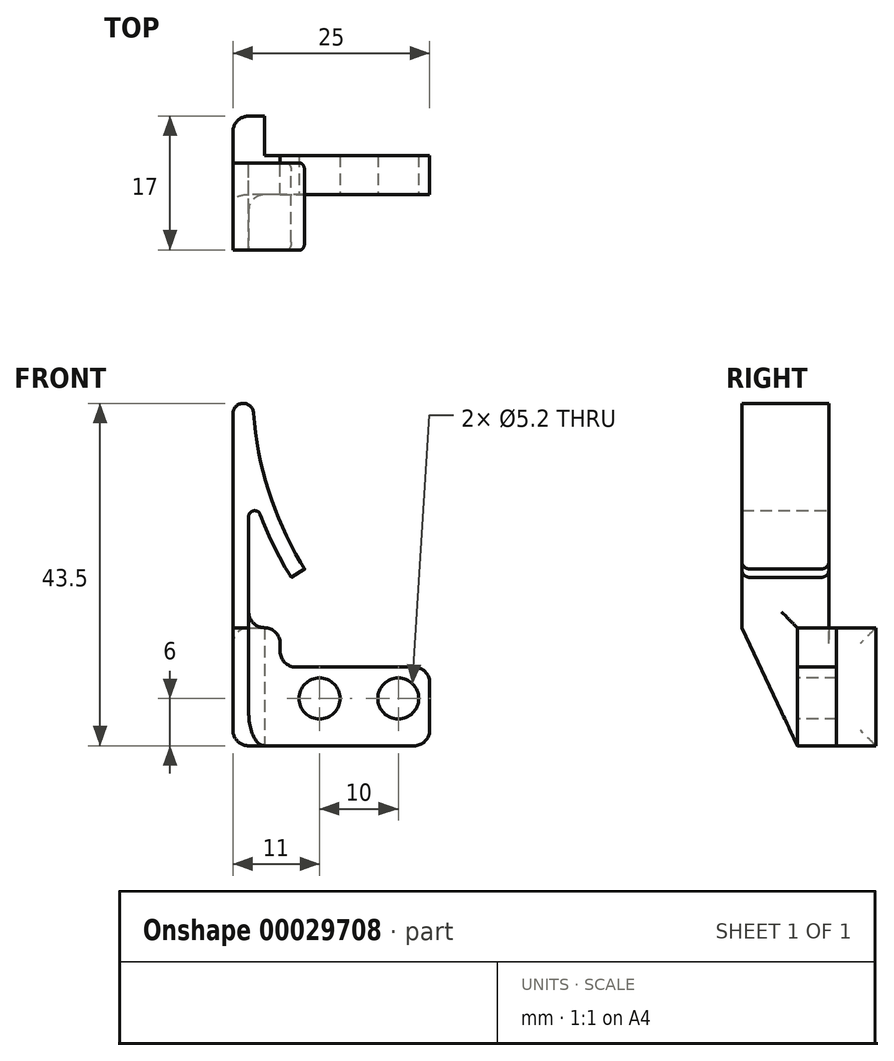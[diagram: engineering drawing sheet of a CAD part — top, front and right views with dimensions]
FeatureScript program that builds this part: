
annotation { "Feature Type Name" : "Feature", "Feature Type Description" : "" }
export const myFeature = defineFeature(function(context is Context, id is Id, definition is map)
    precondition{}
    {
        {
            var Q0;
            Q0=qCreatedBy(makeId("Front.planeOp"),FACE);
            var sketch = newSketch(context, id + "F0", { "sketchPlane" : qUnion([Q0])});
            skLineSegment(sketch, "E0", {"start": v(0, 0) * mm, "end": v(0, 42.19) * mm});
            skLineSegment(sketch, "E1", {"start": v(25, 0) * mm, "end": v(0, 0) * mm});
            skLineSegment(sketch, "E2", {"start": v(2, 29.11) * mm, "end": v(2, 15) * mm});
            skLineSegment(sketch, "E3", {"start": v(2, 15) * mm, "end": v(6, 15) * mm});
            skLineSegment(sketch, "E4", {"start": v(6, 15) * mm, "end": v(6, 10) * mm});
            skLineSegment(sketch, "E5", {"start": v(6, 10) * mm, "end": v(25, 10) * mm});
            skLineSegment(sketch, "E6", {"start": v(46, 0) * mm, "end": v(46, 45.5) * mm, "construction": true});
            skLineSegment(sketch, "E7", {"start": v(46, 45.5) * mm, "end": v(0, 45.5) * mm, "construction": true});
            skLineSegment(sketch, "E8", {"start": v(25, 10) * mm, "end": v(25, 0) * mm});
            skArc(sketch, "E9", {"start": v(2.62, 42.29) * mm, "mid": v(4.66, 31.97) * mm, "end": v(9.1, 22.45) * mm});
            skLineSegment(sketch, "E10", {"start": v(46, 45.5) * mm, "end": v(9.1, 22.45) * mm, "construction": true});
            skArc(sketch, "E11", {"start": v(2.62, 42.29) * mm, "mid": v(1.26, 43.5) * mm, "end": v(0, 42.19) * mm});
            skArc(sketch, "E12", {"start": v(3.45, 29.38) * mm, "mid": v(5.24, 25.29) * mm, "end": v(7.41, 21.39) * mm});
            skLineSegment(sketch, "E13", {"start": v(9.1, 22.45) * mm, "end": v(7.41, 21.39) * mm});
            skLineSegment(sketch, "E14", {"start": v(2.75, 29.11) * mm, "end": v(46, 45.5) * mm, "construction": true});
            skLineSegment(sketch, "E15", {"start": v(2.75, 29.11) * mm, "end": v(46, 29.11) * mm, "construction": true});
            skArc(sketch, "E16", {"start": v(3.45, 29.38) * mm, "mid": v(2.61, 29.85) * mm, "end": v(2, 29.11) * mm});
            skLineSegment(sketch, "E17", {"start": v(1.31, 42.19) * mm, "end": v(46, 45.5) * mm, "construction": true});
            skLineSegment(sketch, "E18", {"start": v(1.31, 42.19) * mm, "end": v(46, 42.19) * mm, "construction": true});
            skSolve(sketch);
        }
        {
            var Q0;
            Q0=makeQuery(id+"F0.imprint","IMPRINT",FACE,{"disambiguationData":[TD([[makeQuery(id+"F0.imprint","IMPRINT",EDGE,{"derivedFrom":sQuery(id+"F0.wireOp",EDGE,"E0")}),-1.0]])]});
            extrude(context, id + "F1", {"entities" : qUnion([Q0]), "depth" : 12 * mm});
        }
        {
            var Q0;
            Q0=makeQuery(id+"F1.opExtrude","CAP_FACE",FACE,{"disambiguationData":[OSD([sQuery(id+"F0.wireOp",EDGE,"E0"),sQuery(id+"F0.wireOp",EDGE,"b13cdfa3-eb26-4a5b-9c51-0565e7d605f8"),sQuery(id+"F0.wireOp",EDGE,"20c8e588-8513-4586-873b-a1e2a7cb5edc"),sQuery(id+"F0.wireOp",EDGE,"99ee8a31-633d-4312-811c-a954296da4b5"),sQuery(id+"F0.wireOp",EDGE,"e968206b-c05c-4754-84ed-d64e79b235ea"),sQuery(id+"F0.wireOp",EDGE,"b45f21d6-cdd7-40ae-9b71-acff4328d14c"),sQuery(id+"F0.wireOp",EDGE,"3f474ec2-51ba-4bb6-b08a-34516dbad5d3"),sQuery(id+"F0.wireOp",EDGE,"E1"),sQuery(id+"F0.wireOp",EDGE,"086c25bb-8a97-4a79-a392-a81f9e8244d4.filletArc"),sQuery(id+"F0.wireOp",EDGE,"f96bd52e-1912-4527-b69c-6590beda2ba5.filletArc")])],"isStart":false});
            var sketch = newSketch(context, id + "F2", { "sketchPlane" : qUnion([Q0])});
            skPoint(sketch, "E19", {"position": v(11, 6) * mm});
            skPoint(sketch, "E20", {"position": v(21, 6) * mm});
            skSolve(sketch);
        }
        {
            var Q0;
            Q0=sQuery(id+"F2.wireOp",VERTEX,"E20");
            var Q1;
            Q1=sQuery(id+"F2.wireOp",VERTEX,"E19");
            var Q2;
            Q2=makeQuery(id+"F1.opExtrude","SWEPT_BODY",BODY,{"disambiguationData":[OSD([sQuery(id+"F0.wireOp",EDGE,"E0"),sQuery(id+"F0.wireOp",EDGE,"b13cdfa3-eb26-4a5b-9c51-0565e7d605f8"),sQuery(id+"F0.wireOp",EDGE,"20c8e588-8513-4586-873b-a1e2a7cb5edc"),sQuery(id+"F0.wireOp",EDGE,"99ee8a31-633d-4312-811c-a954296da4b5"),sQuery(id+"F0.wireOp",EDGE,"3f474ec2-51ba-4bb6-b08a-34516dbad5d3"),sQuery(id+"F0.wireOp",EDGE,"E1"),sQuery(id+"F0.wireOp",EDGE,"086c25bb-8a97-4a79-a392-a81f9e8244d4.filletArc"),sQuery(id+"F0.wireOp",EDGE,"f96bd52e-1912-4527-b69c-6590beda2ba5.filletArc"),sQuery(id+"F0.wireOp",EDGE,"E2"),sQuery(id+"F0.wireOp",EDGE,"E3"),sQuery(id+"F0.wireOp",EDGE,"E4"),sQuery(id+"F0.wireOp",EDGE,"E5")])]});
            hole(context, id + "F3", {"style" : HoleStyle.SIMPLE, "holeDiameter" : 5.2 * mm, "endStyle" : HoleEndStyle.THROUGH, "locations" : qUnion([Q0, Q1]), "scope" : qUnion([Q2])});
        }
        {
            var Q0;
            Q0=makeQuery(id+"F1.opExtrude","CAP_FACE",FACE,{"disambiguationData":[OSD([sQuery(id+"F0.wireOp",EDGE,"E0"),sQuery(id+"F0.wireOp",EDGE,"b13cdfa3-eb26-4a5b-9c51-0565e7d605f8"),sQuery(id+"F0.wireOp",EDGE,"20c8e588-8513-4586-873b-a1e2a7cb5edc"),sQuery(id+"F0.wireOp",EDGE,"99ee8a31-633d-4312-811c-a954296da4b5"),sQuery(id+"F0.wireOp",EDGE,"3f474ec2-51ba-4bb6-b08a-34516dbad5d3"),sQuery(id+"F0.wireOp",EDGE,"E1"),sQuery(id+"F0.wireOp",EDGE,"086c25bb-8a97-4a79-a392-a81f9e8244d4.filletArc"),sQuery(id+"F0.wireOp",EDGE,"f96bd52e-1912-4527-b69c-6590beda2ba5.filletArc"),sQuery(id+"F0.wireOp",EDGE,"E2"),sQuery(id+"F0.wireOp",EDGE,"E3"),sQuery(id+"F0.wireOp",EDGE,"E4"),sQuery(id+"F0.wireOp",EDGE,"E5")])],"isStart":false});
            var sketch = newSketch(context, id + "F4", { "sketchPlane" : qUnion([Q0])});
            skLineSegment(sketch, "E21.bottom", {"start": v(2, 0) * mm, "end": v(0, 0) * mm});
            skLineSegment(sketch, "E21.top", {"start": v(2, 15) * mm, "end": v(0, 15) * mm});
            skLineSegment(sketch, "E21.left", {"start": v(0, 0) * mm, "end": v(0, 15) * mm});
            skLineSegment(sketch, "E21.right", {"start": v(2, 0) * mm, "end": v(2, 15) * mm});
            skSolve(sketch);
        }
        {
            var Q0;
            {var subQ2=sQuery(id+"F4.wireOp",EDGE,"E21.right");Q0=makeQuery(id+"F4.imprint","IMPRINT",FACE,{"disambiguationData":[TD([[makeQuery(id+"F4.imprint","IMPRINT",EDGE,{"derivedFrom":subQ2}),-1.0]])]});}
            extrude(context, id + "F5", {"entities" : qUnion([Q0]), "operationType" : NewBodyOperationType.REMOVE, "oppositeDirection" : true, "depth" : 7 * mm});
        }
        {
            var Q0;
            Q0=makeQuery(id+"F1.opExtrude","SWEPT_FACE",FACE,{"disambiguationData":[OSD([sQuery(id+"F0.wireOp",EDGE,"E0")])]});
            var sketch = newSketch(context, id + "F6", { "sketchPlane" : qUnion([Q0])});
            skLineSegment(sketch, "E22", {"start": v(12, 0) * mm, "end": v(12, 15) * mm});
            skLineSegment(sketch, "E23", {"start": v(12, 15) * mm, "end": v(5, 0) * mm});
            skLineSegment(sketch, "E24", {"start": v(5, 0) * mm, "end": v(12, 0) * mm});
            skSolve(sketch);
        }
        {
            var Q0;
            Q0 = qSketchRegion(id + "F6", true);
            var Q1;
            Q1=makeQuery(id+"F6.imprint","IMPRINT",FACE,{"disambiguationData":[TD([[makeQuery(id+"F6.imprint","IMPRINT",EDGE,{"derivedFrom":sQuery(id+"F6.wireOp",EDGE,"E22")}),1.0]])]});
            extrude(context, id + "F7", {"entities" : qUnion([Q0, Q1]), "operationType" : NewBodyOperationType.REMOVE, "oppositeDirection" : true, "depth" : 3 * mm});
        }
        {
            var Q0;
            Q0=qCreatedBy(makeId("Front.planeOp"),FACE);
            var sketch = newSketch(context, id + "F8", { "sketchPlane" : qUnion([Q0])});
            skLineSegment(sketch, "E25.bottom", {"start": v(-9.17, 45.96) * mm, "end": v(17.7, 45.96) * mm});
            skLineSegment(sketch, "E25.top", {"start": v(-9.17, 15) * mm, "end": v(17.7, 15) * mm});
            skLineSegment(sketch, "E25.left", {"start": v(-9.17, 45.96) * mm, "end": v(-9.17, 15) * mm});
            skLineSegment(sketch, "E25.right", {"start": v(17.7, 45.96) * mm, "end": v(17.7, 15) * mm});
            skSolve(sketch);
        }
        {
            var Q0;
            Q0=makeQuery(id+"F8.imprint","IMPRINT",FACE,{"disambiguationData":[TD([[makeQuery(id+"F8.imprint","IMPRINT",EDGE,{"derivedFrom":sQuery(id+"F8.wireOp",EDGE,"E25.bottom")}),-1.0]])]});
            extrude(context, id + "F9", {"entities" : qUnion([Q0]), "operationType" : NewBodyOperationType.REMOVE, "depth" : 1 * mm});
        }
        {
            var Q0;
            Q0=makeQuery(id+"F1.opExtrude","CAP_FACE",FACE,{"disambiguationData":[OSD([sQuery(id+"F0.wireOp",EDGE,"E0"),sQuery(id+"F0.wireOp",EDGE,"E1"),sQuery(id+"F0.wireOp",EDGE,"E2"),sQuery(id+"F0.wireOp",EDGE,"E3"),sQuery(id+"F0.wireOp",EDGE,"E4"),sQuery(id+"F0.wireOp",EDGE,"E5"),sQuery(id+"F0.wireOp",EDGE,"E8"),sQuery(id+"F0.wireOp",EDGE,"E9"),sQuery(id+"F0.wireOp",EDGE,"E11"),sQuery(id+"F0.wireOp",EDGE,"E12"),sQuery(id+"F0.wireOp",EDGE,"E13"),sQuery(id+"F0.wireOp",EDGE,"E16")])],"isStart":true});
            var sketch = newSketch(context, id + "F10", { "sketchPlane" : qUnion([Q0])});
            skLineSegment(sketch, "E26.bottom", {"start": v(0, 15) * mm, "end": v(-4, 15) * mm});
            skLineSegment(sketch, "E26.top", {"start": v(0, 0) * mm, "end": v(-4, 0) * mm});
            skLineSegment(sketch, "E26.left", {"start": v(0, 15) * mm, "end": v(0, 0) * mm});
            skLineSegment(sketch, "E26.right", {"start": v(-4, 15) * mm, "end": v(-4, 0) * mm});
            skSolve(sketch);
        }
        {
            var Q0;
            {var subQ4=sQuery(id+"F10.wireOp",EDGE,"E26.bottom");Q0=makeQuery(id+"F10.imprint","IMPRINT",FACE,{"disambiguationData":[TD([[makeQuery(id+"F10.imprint","IMPRINT",EDGE,{"derivedFrom":subQ4}),1.0]])]});}
            extrude(context, id + "F11", {"entities" : qUnion([Q0]), "operationType" : NewBodyOperationType.ADD, "depth" : 5 * mm});
        }
        {
            var Q0;
            Q0=makeQuery(id+"F1.opExtrude","CAP_EDGE",EDGE,{"disambiguationData":[OSD([sQuery(id+"F0.wireOp",EDGE,"E13")])],"isStart":false});
            var Q1;
            Q1=makeQuery(id+"F9.boolean.opBoolean","INTERSECT",EDGE,{"derivedFrom":[makeQuery(id+"F1.opExtrude","SWEPT_FACE",FACE,{"disambiguationData":[OSD([sQuery(id+"F0.wireOp",EDGE,"E13")])]}),makeQuery(id+"F9.opExtrude","CAP_FACE",FACE,{"disambiguationData":[OSD([sQuery(id+"F8.wireOp",EDGE,"E25.bottom"),sQuery(id+"F8.wireOp",EDGE,"E25.top"),sQuery(id+"F8.wireOp",EDGE,"E25.left"),sQuery(id+"F8.wireOp",EDGE,"E25.right")])],"isStart":false})]});
            fillet(context, id + "F12", {"entities" : qUnion([Q0, Q1]), "radius" : 1 * mm, "tangentPropagation" : true, "allowEdgeOverflow" : false});
        }
        {
            var Q0;
            Q0=makeQuery(id+"F1.opExtrude","SWEPT_EDGE",EDGE,{"disambiguationData":[OSD([sQuery(id+"F0.wireOp",EDGE,"E0"),sQuery(id+"F0.wireOp",EDGE,"E1")])]});
            var Q1;
            Q1=makeQuery(id+"F1.opExtrude","SWEPT_EDGE",EDGE,{"disambiguationData":[OSD([sQuery(id+"F0.wireOp",EDGE,"E1"),sQuery(id+"F0.wireOp",EDGE,"E8")])]});
            var Q2;
            Q2=makeQuery(id+"F1.opExtrude","SWEPT_EDGE",EDGE,{"disambiguationData":[OSD([sQuery(id+"F0.wireOp",EDGE,"E5"),sQuery(id+"F0.wireOp",EDGE,"E8")])]});
            var Q3;
            Q3=makeQuery(id+"F7.boolean.opBoolean","COPY",EDGE,{"derivedFrom":makeQuery(id+"F7.opExtrude","SWEPT_EDGE",EDGE,{"disambiguationData":[OSD([sQuery(id+"F0.wireOp",EDGE,"E0"),sQuery(id+"F6.wireOp",EDGE,"E22"),sQuery(id+"F6.wireOp",EDGE,"E23")])]})});
            var Q4;
            Q4=makeQuery(id+"F1.opExtrude","SWEPT_EDGE",EDGE,{"disambiguationData":[OSD([sQuery(id+"F0.wireOp",EDGE,"E3"),sQuery(id+"F0.wireOp",EDGE,"E4")])]});
            var Q5;
            Q5=makeQuery(id+"F1.opExtrude","SWEPT_EDGE",EDGE,{"disambiguationData":[OSD([sQuery(id+"F0.wireOp",EDGE,"E4"),sQuery(id+"F0.wireOp",EDGE,"E5")])]});
            var Q6;
            Q6=makeQuery(id+"F1.opExtrude","SWEPT_EDGE",EDGE,{"disambiguationData":[OSD([sQuery(id+"F0.wireOp",EDGE,"E2"),sQuery(id+"F0.wireOp",EDGE,"E3")])]});
            var Q7;
            Q7=makeQuery(id+"F5.boolean.opBoolean","COPY",EDGE,{"derivedFrom":makeQuery(id+"F5.opExtrude","CAP_EDGE",EDGE,{"disambiguationData":[OSD([sQuery(id+"F4.wireOp",EDGE,"E21.right")])],"isStart":false})});
            var Q8;
            Q8=makeQuery(id+"F11.opExtrude","CAP_EDGE",EDGE,{"disambiguationData":[OSD([sQuery(id+"F10.wireOp",EDGE,"E26.left")])],"isStart":false});
            var Q9;
            Q9=makeQuery(id+"F11.boolean.opBoolean","MERGE",EDGE,{"derivedFrom":[makeQuery(id+"F9.boolean.opBoolean","INTERSECT",EDGE,{"derivedFrom":[makeQuery(id+"F1.opExtrude","SWEPT_FACE",FACE,{"disambiguationData":[OSD([sQuery(id+"F0.wireOp",EDGE,"E0")])]}),makeQuery(id+"F9.opExtrude","SWEPT_FACE",FACE,{"disambiguationData":[OSD([sQuery(id+"F8.wireOp",EDGE,"E25.top")])]})]}),makeQuery(id+"F11.opExtrude","SWEPT_EDGE",EDGE,{"disambiguationData":[OSD([sQuery(id+"F10.wireOp",EDGE,"E26.bottom"),sQuery(id+"F10.wireOp",EDGE,"E26.left")])]})]});
            fillet(context, id + "F13", {"entities" : qUnion([Q0, Q1, Q2, Q3, Q4, Q5, Q6, Q7, Q8, Q9]), "radius" : 2 * mm, "tangentPropagation" : true, "allowEdgeOverflow" : false});
        }
    });
